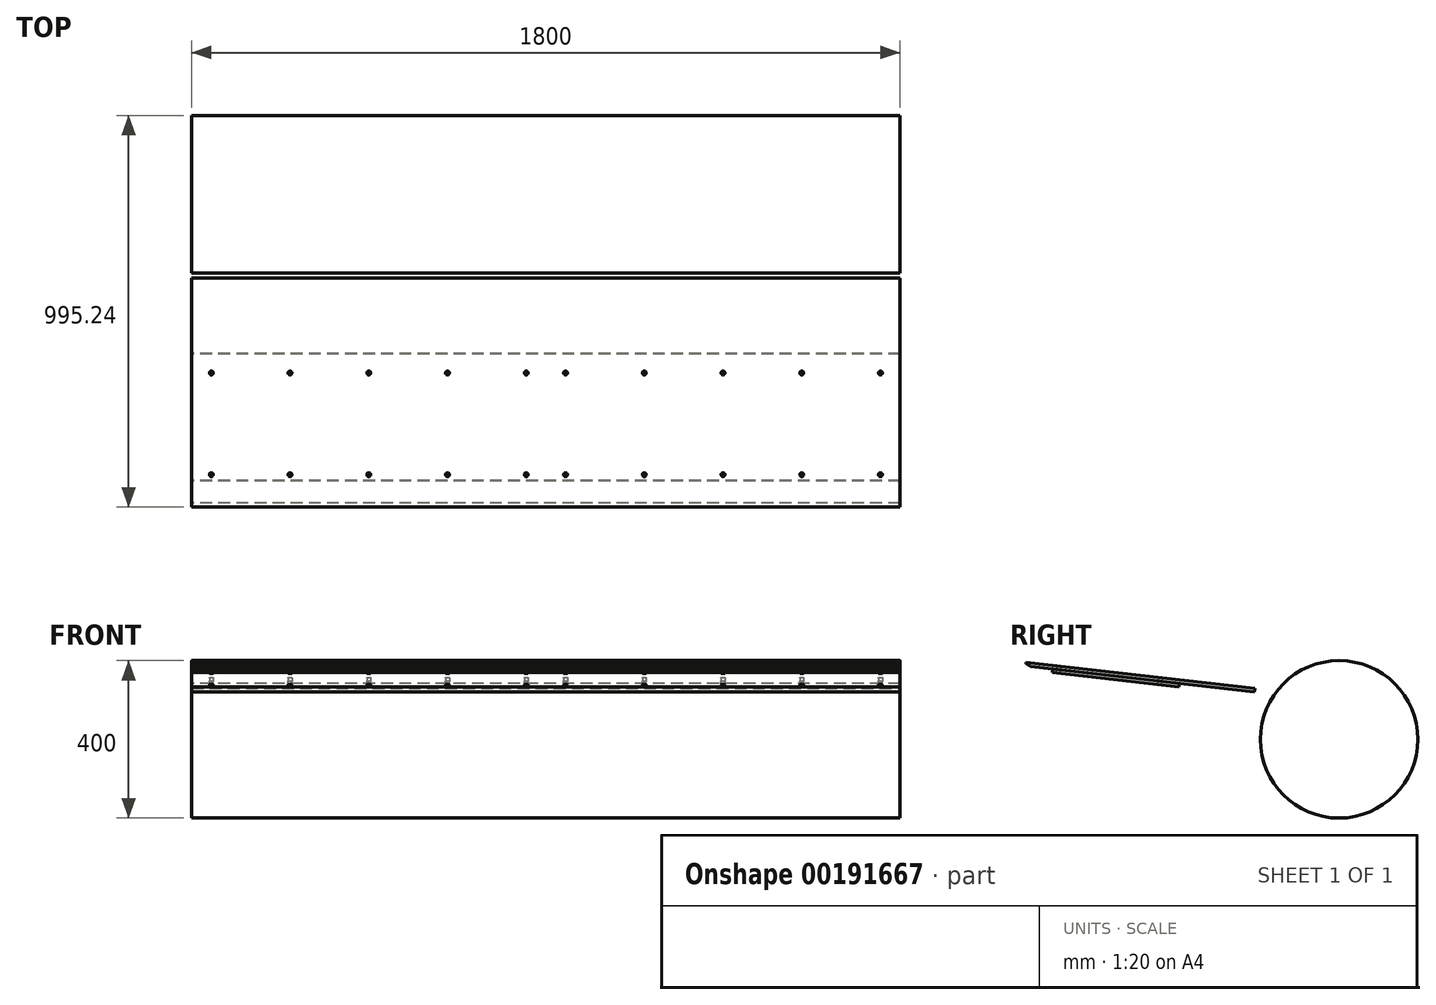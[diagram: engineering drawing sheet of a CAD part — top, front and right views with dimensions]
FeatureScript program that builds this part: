
annotation { "Feature Type Name" : "Feature", "Feature Type Description" : "" }
export const myFeature = defineFeature(function(context is Context, id is Id, definition is map)
    precondition{}
    {
        {
            var Q0;
            Q0=qCreatedBy(makeId("Right.planeOp"),FACE);
            var sketch = newSketch(context, id + "F0", { "sketchPlane" : qUnion([Q0])});
            skLineSegment(sketch, "E0", {"start": v(-122.23, 0) * mm, "end": v(121.2, 0) * mm, "construction": true});
            skLineSegment(sketch, "E1", {"start": v(0, -87.3) * mm, "end": v(0, 103.4) * mm, "construction": true});
            skLineSegment(sketch, "E2.0", {"start": v(-122.23, 117.2) * mm, "end": v(160.5, 117.2) * mm, "construction": true});
            skLineSegment(sketch, "E3.0", {"start": v(160.5, -87.3) * mm, "end": v(160.5, 117.2) * mm, "construction": true});
            skLineSegment(sketch, "E4.0", {"start": v(-161.4, 153.9) * mm, "end": v(121.2, 153.9) * mm, "construction": true});
            skLineSegment(sketch, "E5.0", {"start": v(-161.4, -87.3) * mm, "end": v(-161.4, 153.9) * mm, "construction": true});
            skLineSegment(sketch, "E6", {"start": v(-161.4, 153.9) * mm, "end": v(160.5, 117.2) * mm});
            skLineSegment(sketch, "E7.0", {"start": v(-162.42, 144.96) * mm, "end": v(159.48, 108.26) * mm});
            skLineSegment(sketch, "E8", {"start": v(-162.42, 144.96) * mm, "end": v(-161.4, 153.9) * mm});
            skLineSegment(sketch, "E9", {"start": v(159.48, 108.26) * mm, "end": v(160.5, 117.2) * mm});
            skSolve(sketch);
        }
        {
            var Q0;
            Q0=makeQuery(id+"F0.imprint","IMPRINT",FACE,{"disambiguationData":[TD([[makeQuery(id+"F0.imprint","IMPRINT",EDGE,{"derivedFrom":sQuery(id+"F0.wireOp",EDGE,"E6")}),-1.0]])]});
            extrude(context, id + "F1", {"entities" : qUnion([Q0]), "endBound" : BoundingType.SYMMETRIC, "depth" : 1800 * mm});
        }
        {
            var Q0;
            Q0=makeQuery(id+"F1.opExtrude","SWEPT_FACE",FACE,{"disambiguationData":[OSD([sQuery(id+"F0.wireOp",EDGE,"E6")])]});
            var sketch = newSketch(context, id + "F2", { "sketchPlane" : qUnion([Q0])});
            skLineSegment(sketch, "E10.0", {"start": v(900, 146.2) * mm, "end": v(-900, 146.2) * mm, "construction": true});
            skLineSegment(sketch, "E11.0", {"start": v(900, 96.2) * mm, "end": v(-900, 96.2) * mm, "construction": true});
            skLineSegment(sketch, "E12.0", {"start": v(900, -163.8) * mm, "end": v(-900, -163.8) * mm, "construction": true});
            skLineSegment(sketch, "E13", {"start": v(0, -292.8) * mm, "end": v(0, 273.7) * mm, "construction": true});
            skLineSegment(sketch, "E14.0", {"start": v(-50, -292.8) * mm, "end": v(-50, 273.7) * mm, "construction": true});
            skPoint(sketch, "E15", {"position": v(-50, -163.8) * mm});
            skPoint(sketch, "E16", {"position": v(-50, 96.2) * mm});
            skPoint(sketch, "E17.1.0.0", {"position": v(-250, 96.2) * mm});
            skPoint(sketch, "E17.1.0.1", {"position": v(-250, -163.8) * mm});
            skPoint(sketch, "E17.2.0.0", {"position": v(-450, 96.2) * mm});
            skPoint(sketch, "E17.2.0.1", {"position": v(-450, -163.8) * mm});
            skPoint(sketch, "E17.3.0.0", {"position": v(-650, 96.2) * mm});
            skPoint(sketch, "E17.3.0.1", {"position": v(-650, -163.8) * mm});
            skPoint(sketch, "E17.4.0.0", {"position": v(-850, 96.2) * mm});
            skPoint(sketch, "E17.4.0.1", {"position": v(-850, -163.8) * mm});
            skLineSegment(sketch, "E17.direction1", {"start": v(-50, -163.8) * mm, "end": v(-250, -163.8) * mm, "construction": true});
            skPoint(sketch, "E18.MirrorP", {"position": v(50, -163.8) * mm});
            skPoint(sketch, "E19.MirrorP", {"position": v(450, -163.8) * mm});
            skPoint(sketch, "E20.MirrorP", {"position": v(250, -163.8) * mm});
            skPoint(sketch, "E21.MirrorP", {"position": v(650, -163.8) * mm});
            skPoint(sketch, "E22.MirrorP", {"position": v(850, -163.8) * mm});
            skPoint(sketch, "E23.MirrorP", {"position": v(250, 96.2) * mm});
            skPoint(sketch, "E24.MirrorP", {"position": v(650, 96.2) * mm});
            skPoint(sketch, "E25.MirrorP", {"position": v(450, 96.2) * mm});
            skPoint(sketch, "E26.MirrorP", {"position": v(850, 96.2) * mm});
            skPoint(sketch, "E27.MirrorP", {"position": v(50, 96.2) * mm});
            skLineSegment(sketch, "E28.MirrorCS", {"start": v(50, -163.8) * mm, "end": v(250, -163.8) * mm, "construction": true});
            skSolve(sketch);
        }
        {
            var Q0;
            Q0=sQuery(id+"F2.wireOp",VERTEX,"E22.MirrorP");
            var Q1;
            Q1=sQuery(id+"F2.wireOp",VERTEX,"E21.MirrorP");
            var Q2;
            Q2=sQuery(id+"F2.wireOp",VERTEX,"E19.MirrorP");
            var Q3;
            Q3=sQuery(id+"F2.wireOp",VERTEX,"E20.MirrorP");
            var Q4;
            Q4=sQuery(id+"F2.wireOp",VERTEX,"E18.MirrorP");
            var Q5;
            Q5=sQuery(id+"F2.wireOp",VERTEX,"E15");
            var Q6;
            Q6=sQuery(id+"F2.wireOp",VERTEX,"E17.1.0.1");
            var Q7;
            Q7=sQuery(id+"F2.wireOp",VERTEX,"E17.2.0.1");
            var Q8;
            Q8=sQuery(id+"F2.wireOp",VERTEX,"E17.3.0.1");
            var Q9;
            Q9=sQuery(id+"F2.wireOp",VERTEX,"E17.4.0.1");
            var Q10;
            Q10=sQuery(id+"F2.wireOp",VERTEX,"E17.4.0.0");
            var Q11;
            Q11=sQuery(id+"F2.wireOp",VERTEX,"E17.3.0.0");
            var Q12;
            Q12=sQuery(id+"F2.wireOp",VERTEX,"E17.2.0.0");
            var Q13;
            Q13=sQuery(id+"F2.wireOp",VERTEX,"E17.1.0.0");
            var Q14;
            Q14=sQuery(id+"F2.wireOp",VERTEX,"E16");
            var Q15;
            Q15=sQuery(id+"F2.wireOp",VERTEX,"E27.MirrorP");
            var Q16;
            Q16=sQuery(id+"F2.wireOp",VERTEX,"E23.MirrorP");
            var Q17;
            Q17=sQuery(id+"F2.wireOp",VERTEX,"E25.MirrorP");
            var Q18;
            Q18=sQuery(id+"F2.wireOp",VERTEX,"E24.MirrorP");
            var Q19;
            Q19=sQuery(id+"F2.wireOp",VERTEX,"E26.MirrorP");
            var Q20;
            Q20=makeQuery(id+"F1.opExtrude","SWEPT_BODY",BODY,{"disambiguationData":[OSD([sQuery(id+"F0.wireOp",EDGE,"E6"),sQuery(id+"F0.wireOp",EDGE,"E7.0"),sQuery(id+"F0.wireOp",EDGE,"E8"),sQuery(id+"F0.wireOp",EDGE,"E9")])]});
            hole(context, id + "F3", {"style" : HoleStyle.SIMPLE, "endStyle" : HoleEndStyle.THROUGH, "standardTappedOrClearance" : lookupTablePath({ "standard" : "ISO", "size" : "9.5", "type" : "Drilled" }), "standardBlindInLast" : lookupTablePath({ "standard" : "ISO", "size" : "9.5", "type" : "Drilled" }), "holeDiameter" : 9.5 * mm, "locations" : qUnion([Q0, Q1, Q2, Q3, Q4, Q5, Q6, Q7, Q8, Q9, Q10, Q11, Q12, Q13, Q14, Q15, Q16, Q17, Q18, Q19]), "scope" : qUnion([Q20]), "isTappedThrough" : true});
        }
        {
            var Q0;
            Q0=makeQuery(id+"F1.opExtrude","SWEPT_FACE",FACE,{"disambiguationData":[OSD([sQuery(id+"F0.wireOp",EDGE,"E6")])]});
            var sketch = newSketch(context, id + "F4", { "sketchPlane" : qUnion([Q0])});
            skLineSegment(sketch, "E29", {"start": v(850, -163.8) * mm, "end": v(-850.32, -163.8) * mm, "construction": true});
            skLineSegment(sketch, "E30", {"start": v(-850, 96.2) * mm, "end": v(850, 96.2) * mm, "construction": true});
            skLineSegment(sketch, "E31.0", {"start": v(900, -246.8) * mm, "end": v(-900, -246.8) * mm});
            skLineSegment(sketch, "E32.0", {"start": v(-900, 338.2) * mm, "end": v(900, 338.2) * mm});
            skLineSegment(sketch, "E33.0", {"start": v(900, -246.8) * mm, "end": v(900, 338.2) * mm});
            skLineSegment(sketch, "E34.0", {"start": v(-900, -246.8) * mm, "end": v(-900, 338.2) * mm});
            skPoint(sketch, "E35.orphan", {"position": v(900, -177.8) * mm});
            skPoint(sketch, "E36.orphan", {"position": v(900, 146.2) * mm});
            skPoint(sketch, "E37.orphan", {"position": v(-900, -177.8) * mm});
            skPoint(sketch, "E38.orphan", {"position": v(-900, 146.2) * mm});
            skLineSegment(sketch, "E39.0.0", {"start": v(-900, 146.2) * mm, "end": v(-900, -177.8) * mm});
            skLineSegment(sketch, "E39.0.1", {"start": v(-900, -177.8) * mm, "end": v(900, -177.8) * mm});
            skLineSegment(sketch, "E39.0.2", {"start": v(900, -177.8) * mm, "end": v(900, 146.2) * mm});
            skLineSegment(sketch, "E39.0.3", {"start": v(900, 146.2) * mm, "end": v(-900, 146.2) * mm});
            skCircle(sketch, "E40.0", {"center": v(650, -163.8) * mm, "radius": 4.75 * mm});
            skCircle(sketch, "E41.0", {"center": v(450, -163.8) * mm, "radius": 4.75 * mm});
            skCircle(sketch, "E42.0", {"center": v(850, -163.8) * mm, "radius": 4.75 * mm});
            skCircle(sketch, "E43.0", {"center": v(850, 96.2) * mm, "radius": 4.75 * mm});
            skCircle(sketch, "E44.0", {"center": v(650, 96.2) * mm, "radius": 4.75 * mm});
            skCircle(sketch, "E45.0", {"center": v(450, 96.2) * mm, "radius": 4.75 * mm});
            skCircle(sketch, "E46.0", {"center": v(250, 96.2) * mm, "radius": 4.75 * mm});
            skCircle(sketch, "E47.0", {"center": v(250, -163.8) * mm, "radius": 4.75 * mm});
            skCircle(sketch, "E48.0", {"center": v(50, -163.8) * mm, "radius": 4.75 * mm});
            skCircle(sketch, "E49.0", {"center": v(-50, -163.8) * mm, "radius": 4.75 * mm});
            skCircle(sketch, "E50.0", {"center": v(-50, 96.2) * mm, "radius": 4.75 * mm});
            skCircle(sketch, "E51.0", {"center": v(50, 96.2) * mm, "radius": 4.75 * mm});
            skCircle(sketch, "E52.0", {"center": v(-250, -163.8) * mm, "radius": 4.75 * mm});
            skCircle(sketch, "E53.0", {"center": v(-250, 96.2) * mm, "radius": 4.75 * mm});
            skCircle(sketch, "E54.0", {"center": v(-850, 96.2) * mm, "radius": 4.75 * mm});
            skLineSegment(sketch, "E54.2", {"start": v(-900, -177.8) * mm, "end": v(-900, 146.2) * mm});
            skCircle(sketch, "E54.3", {"center": v(-650, 96.2) * mm, "radius": 4.75 * mm});
            skCircle(sketch, "E54.4", {"center": v(-650, 96.2) * mm, "radius": 4.75 * mm});
            skCircle(sketch, "E54.5", {"center": v(-450, 96.2) * mm, "radius": 4.75 * mm});
            skCircle(sketch, "E54.6", {"center": v(-450, 96.2) * mm, "radius": 4.75 * mm});
            skCircle(sketch, "E54.7", {"center": v(-850, 96.2) * mm, "radius": 4.75 * mm});
            skLineSegment(sketch, "E54.9", {"start": v(-900, -177.8) * mm, "end": v(-900, 146.2) * mm});
            skCircle(sketch, "E55.0", {"center": v(-450, -163.8) * mm, "radius": 4.75 * mm});
            skCircle(sketch, "E56.0", {"center": v(-650, -163.8) * mm, "radius": 4.75 * mm});
            skCircle(sketch, "E57.0", {"center": v(-850, -163.8) * mm, "radius": 4.75 * mm});
            skSolve(sketch);
        }
        {
            var Q0;
            Q0 = qSketchRegion(id + "F4", true);
            extrude(context, id + "F5", {"entities" : qUnion([Q0]), "depth" : 9 * mm});
        }
        {
            var Q0;
            Q0=makeQuery(id+"F5.opExtrude","CAP_EDGE",EDGE,{"disambiguationData":[OSD([sQuery(id+"F4.wireOp",EDGE,"E31.0")])],"isStart":true});
            chamfer(context, id + "F6", {"entities" : qUnion([Q0]), "chamferType" : ChamferType.OFFSET_ANGLE, "width" : 12 * mm, "oppositeDirection" : false, "angle" : 30 * degree, "tangentPropagation" : true});
        }
        {
            var Q0;
            Q0=qCreatedBy(makeId("Right.planeOp"),FACE);
            var sketch = newSketch(context, id + "F7", { "sketchPlane" : qUnion([Q0])});
            skLineSegment(sketch, "E58.0", {"start": v(-228.95, 170.66) * mm, "end": v(352.28, 104.4) * mm, "construction": true});
            skLineSegment(sketch, "E59", {"start": v(-228.95, 170.66) * mm, "end": v(-228.95, -310.83) * mm, "construction": true});
            skLineSegment(sketch, "E60", {"start": v(-228.95, 170.66) * mm, "end": v(865.27, 170.66) * mm, "construction": true});
            skLineSegment(sketch, "E61.0", {"start": v(-228.95, 175.16) * mm, "end": v(865.27, 175.16) * mm, "construction": true});
            skLineSegment(sketch, "E62.0", {"start": v(566.05, 170.66) * mm, "end": v(566.05, -310.83) * mm, "construction": true});
            skLineSegment(sketch, "E63.0", {"start": v(-228.95, -24.84) * mm, "end": v(865.27, -24.84) * mm, "construction": true});
            skCircle(sketch, "E64", {"center": v(566.05, -24.84) * mm, "radius": 200 * mm});
            skSolve(sketch);
        }
        {
            var Q0;
            Q0 = qSketchRegion(id + "F7", true);
            extrude(context, id + "F8", {"entities" : qUnion([Q0]), "endBound" : BoundingType.SYMMETRIC, "depth" : 1800 * mm});
        }
    });
